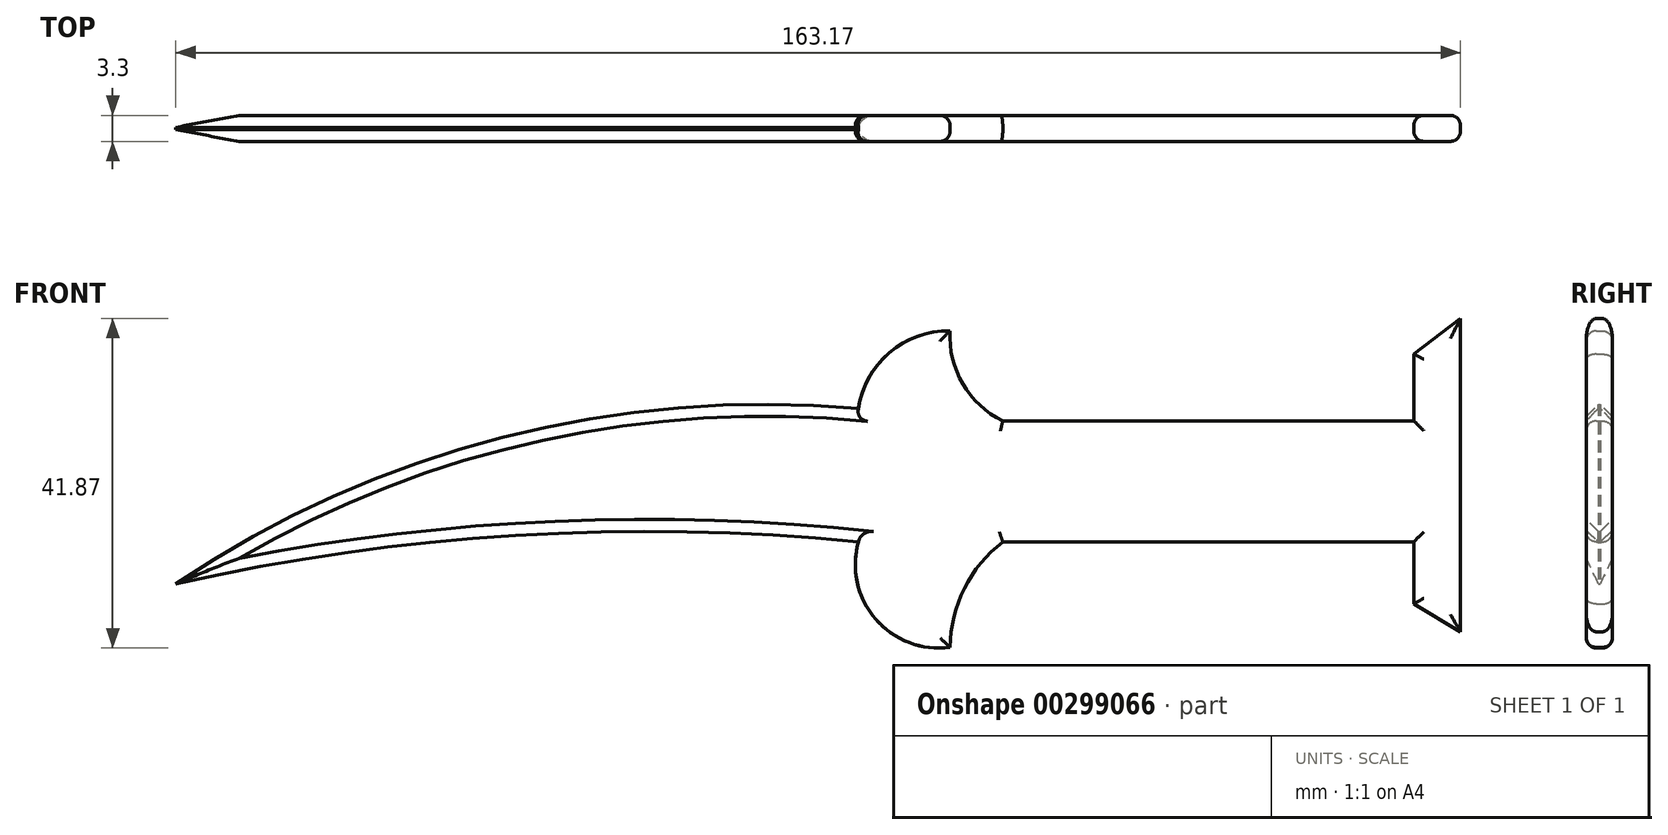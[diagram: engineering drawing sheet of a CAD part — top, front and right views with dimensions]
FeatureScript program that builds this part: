
annotation { "Feature Type Name" : "Feature", "Feature Type Description" : "" }
export const myFeature = defineFeature(function(context is Context, id is Id, definition is map)
    precondition{}
    {
        {
            var Q0;
            Q0=qCreatedBy(makeId("Front.planeOp"),FACE);
            var sketch = newSketch(context, id + "F0", { "sketchPlane" : qUnion([Q0])});
            skLineSegment(sketch, "E0", {"start": v(67.8, -8.47) * mm, "end": v(67.8, 31.33) * mm});
            skLineSegment(sketch, "E1", {"start": v(67.8, 31.33) * mm, "end": v(61.88, 26.8) * mm});
            skLineSegment(sketch, "E2", {"start": v(67.8, -8.47) * mm, "end": v(61.88, -4.93) * mm});
            skLineSegment(sketch, "E3", {"start": v(61.88, -4.93) * mm, "end": v(61.88, 2.96) * mm});
            skLineSegment(sketch, "E4", {"start": v(61.88, 26.8) * mm, "end": v(61.88, 18.33) * mm});
            skLineSegment(sketch, "E5", {"start": v(61.88, 18.33) * mm, "end": v(9.66, 18.33) * mm});
            skLineSegment(sketch, "E6", {"start": v(61.88, 2.96) * mm, "end": v(9.66, 2.96) * mm});
            skArc(sketch, "E7", {"start": v(9.66, 2.96) * mm, "mid": v(4.77, -2.98) * mm, "end": v(2.96, -10.44) * mm});
            skArc(sketch, "E8", {"start": v(-8.67, 2.96) * mm, "mid": v(-6.47, -6.88) * mm, "end": v(2.96, -10.44) * mm});
            skArc(sketch, "E9", {"start": v(-8.67, 2.96) * mm, "mid": v(-52.24, 3.77) * mm, "end": v(-95.38, -2.36) * mm});
            skArc(sketch, "E10", {"start": v(2.96, 29.76) * mm, "mid": v(4.58, 23.03) * mm, "end": v(9.66, 18.33) * mm});
            skArc(sketch, "E11", {"start": v(2.96, 29.76) * mm, "mid": v(-4.7, 27.02) * mm, "end": v(-8.67, 19.9) * mm});
            skArc(sketch, "E12", {"start": v(-8.67, 19.9) * mm, "mid": v(-53.94, 16.2) * mm, "end": v(-95.38, -2.36) * mm});
            skSolve(sketch);
        }
        {
            var Q0;
            Q0 = qSketchRegion(id + "F0", true);
            extrude(context, id + "F1", {"entities" : qUnion([Q0]), "depth" : 3.3 * mm});
        }
        {
            var Q0;
            Q0=makeQuery(id+"F1.opExtrude","CAP_EDGE",EDGE,{"disambiguationData":[OSD([sQuery(id+"F0.wireOp",EDGE,"E10")])],"isStart":true});
            var Q1;
            Q1=makeQuery(id+"F1.opExtrude","CAP_EDGE",EDGE,{"disambiguationData":[OSD([sQuery(id+"F0.wireOp",EDGE,"E10")])],"isStart":false});
            var Q2;
            Q2=makeQuery(id+"F1.opExtrude","CAP_EDGE",EDGE,{"disambiguationData":[OSD([sQuery(id+"F0.wireOp",EDGE,"E7")])],"isStart":false});
            var Q3;
            Q3=makeQuery(id+"F1.opExtrude","CAP_EDGE",EDGE,{"disambiguationData":[OSD([sQuery(id+"F0.wireOp",EDGE,"E7")])],"isStart":true});
            var Q4;
            Q4=makeQuery(id+"F1.opExtrude","CAP_EDGE",EDGE,{"disambiguationData":[OSD([sQuery(id+"F0.wireOp",EDGE,"E6")])],"isStart":false});
            var Q5;
            Q5=makeQuery(id+"F1.opExtrude","CAP_EDGE",EDGE,{"disambiguationData":[OSD([sQuery(id+"F0.wireOp",EDGE,"E5")])],"isStart":false});
            var Q6;
            Q6=makeQuery(id+"F1.opExtrude","CAP_EDGE",EDGE,{"disambiguationData":[OSD([sQuery(id+"F0.wireOp",EDGE,"E5")])],"isStart":true});
            var Q7;
            Q7=makeQuery(id+"F1.opExtrude","CAP_EDGE",EDGE,{"disambiguationData":[OSD([sQuery(id+"F0.wireOp",EDGE,"E6")])],"isStart":true});
            var Q8;
            Q8=makeQuery(id+"F1.opExtrude","CAP_EDGE",EDGE,{"disambiguationData":[OSD([sQuery(id+"F0.wireOp",EDGE,"E0")])],"isStart":true});
            var Q9;
            Q9=makeQuery(id+"F1.opExtrude","CAP_EDGE",EDGE,{"disambiguationData":[OSD([sQuery(id+"F0.wireOp",EDGE,"E2")])],"isStart":true});
            var Q10;
            Q10=makeQuery(id+"F1.opExtrude","CAP_EDGE",EDGE,{"disambiguationData":[OSD([sQuery(id+"F0.wireOp",EDGE,"E3")])],"isStart":true});
            var Q11;
            Q11=makeQuery(id+"F1.opExtrude","CAP_EDGE",EDGE,{"disambiguationData":[OSD([sQuery(id+"F0.wireOp",EDGE,"E1")])],"isStart":true});
            var Q12;
            Q12=makeQuery(id+"F1.opExtrude","CAP_EDGE",EDGE,{"disambiguationData":[OSD([sQuery(id+"F0.wireOp",EDGE,"E4")])],"isStart":true});
            var Q13;
            Q13=makeQuery(id+"F1.opExtrude","CAP_EDGE",EDGE,{"disambiguationData":[OSD([sQuery(id+"F0.wireOp",EDGE,"E4")])],"isStart":false});
            var Q14;
            Q14=makeQuery(id+"F1.opExtrude","CAP_EDGE",EDGE,{"disambiguationData":[OSD([sQuery(id+"F0.wireOp",EDGE,"E1")])],"isStart":false});
            var Q15;
            Q15=makeQuery(id+"F1.opExtrude","CAP_EDGE",EDGE,{"disambiguationData":[OSD([sQuery(id+"F0.wireOp",EDGE,"E0")])],"isStart":false});
            var Q16;
            Q16=makeQuery(id+"F1.opExtrude","CAP_EDGE",EDGE,{"disambiguationData":[OSD([sQuery(id+"F0.wireOp",EDGE,"E2")])],"isStart":false});
            var Q17;
            Q17=makeQuery(id+"F1.opExtrude","CAP_EDGE",EDGE,{"disambiguationData":[OSD([sQuery(id+"F0.wireOp",EDGE,"E3")])],"isStart":false});
            var Q18;
            Q18=makeQuery(id+"F1.opExtrude","CAP_EDGE",EDGE,{"disambiguationData":[OSD([sQuery(id+"F0.wireOp",EDGE,"E11")])],"isStart":false});
            var Q19;
            Q19=makeQuery(id+"F1.opExtrude","CAP_EDGE",EDGE,{"disambiguationData":[OSD([sQuery(id+"F0.wireOp",EDGE,"E11")])],"isStart":true});
            var Q20;
            Q20=makeQuery(id+"F1.opExtrude","CAP_EDGE",EDGE,{"disambiguationData":[OSD([sQuery(id+"F0.wireOp",EDGE,"E8")])],"isStart":false});
            var Q21;
            Q21=makeQuery(id+"F1.opExtrude","CAP_EDGE",EDGE,{"disambiguationData":[OSD([sQuery(id+"F0.wireOp",EDGE,"E8")])],"isStart":true});
            fillet(context, id + "F2", {"entities" : qUnion([Q0, Q1, Q2, Q3, Q4, Q5, Q6, Q7, Q8, Q9, Q10, Q11, Q12, Q13, Q14, Q15, Q16, Q17, Q18, Q19, Q20, Q21]), "radius" : 1.27 * mm, "tangentPropagation" : true, "allowEdgeOverflow" : false});
        }
        {
            var Q0;
            Q0=makeQuery(id+"F1.opExtrude","CAP_EDGE",EDGE,{"disambiguationData":[OSD([sQuery(id+"F0.wireOp",EDGE,"E12")])],"isStart":true});
            var Q1;
            Q1=makeQuery(id+"F1.opExtrude","CAP_EDGE",EDGE,{"disambiguationData":[OSD([sQuery(id+"F0.wireOp",EDGE,"E9")])],"isStart":true});
            var Q2;
            Q2=makeQuery(id+"F1.opExtrude","CAP_EDGE",EDGE,{"disambiguationData":[OSD([sQuery(id+"F0.wireOp",EDGE,"E12")])],"isStart":false});
            var Q3;
            Q3=makeQuery(id+"F1.opExtrude","CAP_EDGE",EDGE,{"disambiguationData":[OSD([sQuery(id+"F0.wireOp",EDGE,"E9")])],"isStart":false});
            chamfer(context, id + "F3", {"entities" : qUnion([Q0, Q1, Q2, Q3]), "width" : 1.52 * mm, "tangentPropagation" : true});
        }
    });
